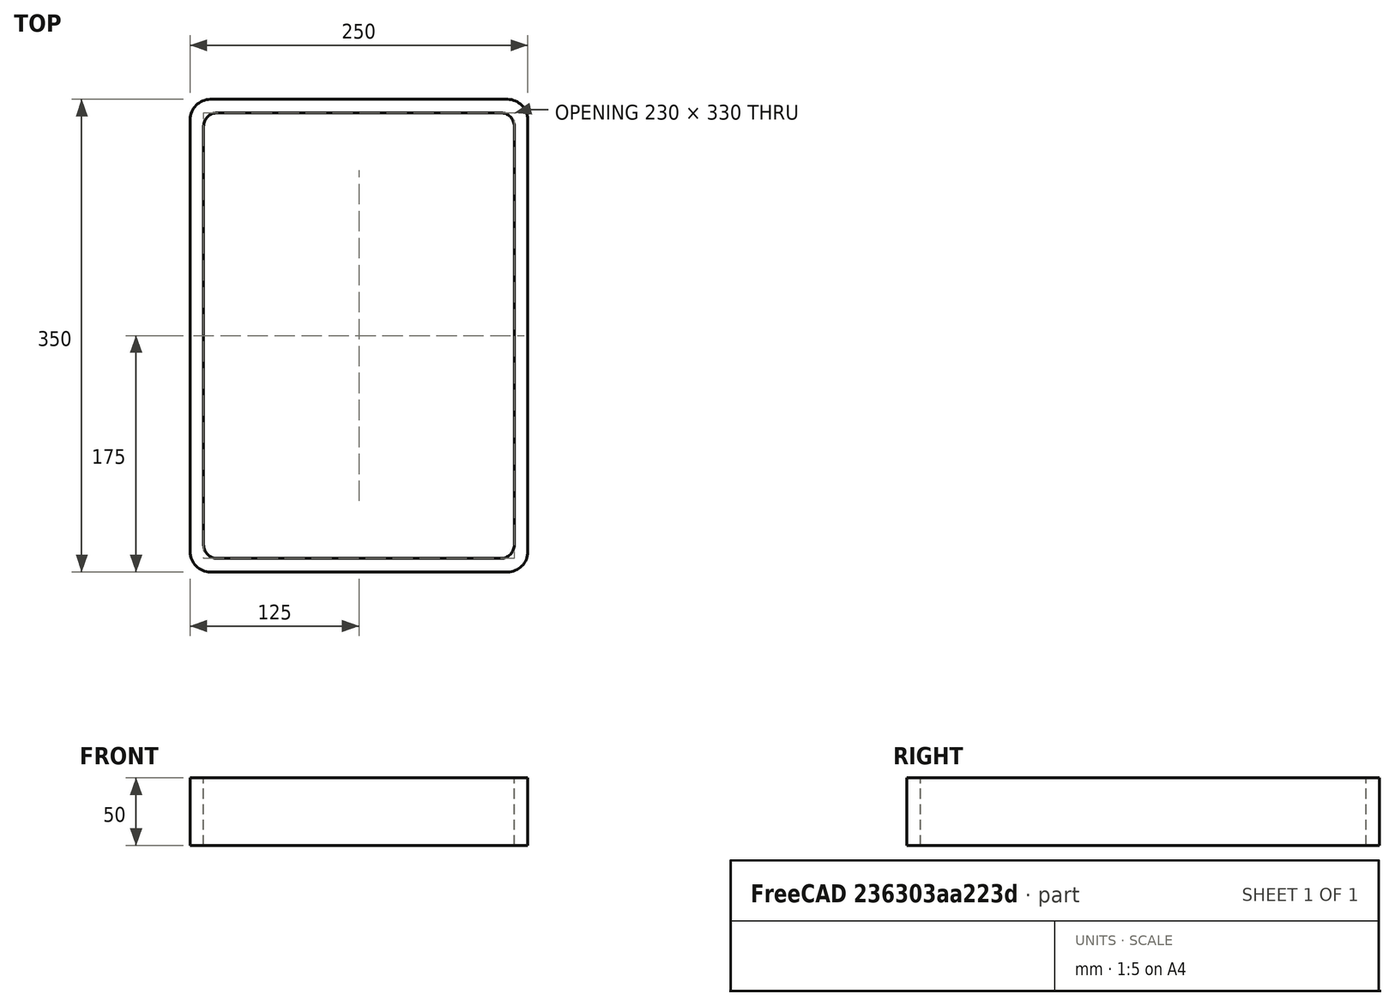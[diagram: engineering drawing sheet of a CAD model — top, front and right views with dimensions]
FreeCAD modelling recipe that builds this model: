
FCSTD DOCUMENT  (FreeCAD 0.15R4671 (Git))
Label: Rectangular hollow section 350x250x10 EN10219 S235JRH
License: All rights reserved
LicenseURL: http://en.wikipedia.org/wiki/All_rights_reserved
objects: Sketcher::SketchObject×1, Part::Extrusion×1
note: 2 computed .brp shape members not serialized (recipe doc carries the construction recipe); baked Part::Feature solids carry a one-line shape summary decoded from their .brp

FEATURE [Sketcher::SketchObject] Sketch
  sketch-geometry (16):
    g0: LineSegment StartX=-105 StartY=165 StartZ=0 EndX=105 EndY=165 EndZ=0
    g1: LineSegment StartX=115 StartY=155 StartZ=0 EndX=115 EndY=-155 EndZ=0
    g2: LineSegment StartX=105 StartY=-165 StartZ=0 EndX=-105 EndY=-165 EndZ=0
    g3: LineSegment StartX=-115 StartY=-155 StartZ=0 EndX=-115 EndY=155 EndZ=0
    g4: LineSegment StartX=-110 StartY=175 StartZ=0 EndX=110 EndY=175 EndZ=0
    g5: LineSegment StartX=125 StartY=160 StartZ=0 EndX=125 EndY=-160 EndZ=0
    g6: LineSegment StartX=110 StartY=-175 StartZ=0 EndX=-110 EndY=-175 EndZ=0
    g7: LineSegment StartX=-125 StartY=-160 StartZ=0 EndX=-125 EndY=160 EndZ=0
    g8: ArcOfCircle CenterX=-105 CenterY=155 CenterZ=0 NormalX=0 NormalY=0 NormalZ=1 Radius=10 StartAngle=1.5708 EndAngle=3.14159
    g9: ArcOfCircle CenterX=105 CenterY=155 CenterZ=0 NormalX=0 NormalY=0 NormalZ=1 Radius=10 StartAngle=0 EndAngle=1.5708
    g10: ArcOfCircle CenterX=105 CenterY=-155 CenterZ=0 NormalX=0 NormalY=0 NormalZ=1 Radius=10 StartAngle=4.71239 EndAngle=6.28319
    g11: ArcOfCircle CenterX=-105 CenterY=-155 CenterZ=0 NormalX=0 NormalY=0 NormalZ=1 Radius=10 StartAngle=3.14159 EndAngle=4.71239
    g12: ArcOfCircle CenterX=110 CenterY=160 CenterZ=0 NormalX=0 NormalY=0 NormalZ=1 Radius=15 StartAngle=0 EndAngle=1.5708
    g13: ArcOfCircle CenterX=110 CenterY=-160 CenterZ=0 NormalX=0 NormalY=0 NormalZ=1 Radius=15 StartAngle=4.71239 EndAngle=6.28319
    g14: ArcOfCircle CenterX=-110 CenterY=-160 CenterZ=0 NormalX=0 NormalY=0 NormalZ=1 Radius=15 StartAngle=3.14159 EndAngle=4.71239
    g15: ArcOfCircle CenterX=-110 CenterY=160 CenterZ=0 NormalX=0 NormalY=0 NormalZ=1 Radius=15 StartAngle=1.5708 EndAngle=3.14159
  constraints (36):
    c: Horizontal(g2)
    c: Vertical(g3)
    c: Horizontal(g6)
    c: Vertical(g7)
    c: Tangent(g3,g8) = 1.5708
    c: Tangent(g0,g8) = 1.5708
    c: Tangent(g0,g9) = 1.5708
    c: Tangent(g1,g9) = 1.5708
    c: Tangent(g1,g10) = 1.5708
    c: Tangent(g2,g10) = 1.5708
    c: Tangent(g2,g11) = 1.5708
    c: Tangent(g3,g11) = 1.5708
    c: Tangent(g4,g12) = 1.5708
    c: Tangent(g5,g12) = 1.5708
    c: Tangent(g5,g13) = 1.5708
    c: Tangent(g6,g13) = 1.5708
    c: Tangent(g6,g14) = 1.5708
    c: Tangent(g7,g14) = 1.5708
    c: Tangent(g7,g15) = 1.5708
    c: Tangent(g4,g15) = 1.5708
    c: Equal(g9,g8)
    c: Equal(g9,g11)
    c: Equal(g9,g10)
    c: Equal(g12,g15)
    c: Equal(g12,g14)
    c: Equal(g12,g13)
    c: Symmetric(g4,g6,g-1)
    c: Symmetric(g7,g5,g-2)
    c: DistanceY(g4,g6) = -350
    c: DistanceX(g7,g5) = 250
    c: Symmetric(g3,g1,g-2)
    c: Symmetric(g0,g2,g-1)
    c: DistanceY(g0,g4) = 10
    c: DistanceX(g5,g1) = -10
    c: Radius(g9) = 10
    c: Radius(g12) = 15
FEATURE [Part::Extrusion] Extrude  label="Rectangular hollow section 350x250x10 EN10219 S235JRH"
  Base = -> Sketch
  Dir = (0,0,50)
  Solid = true
